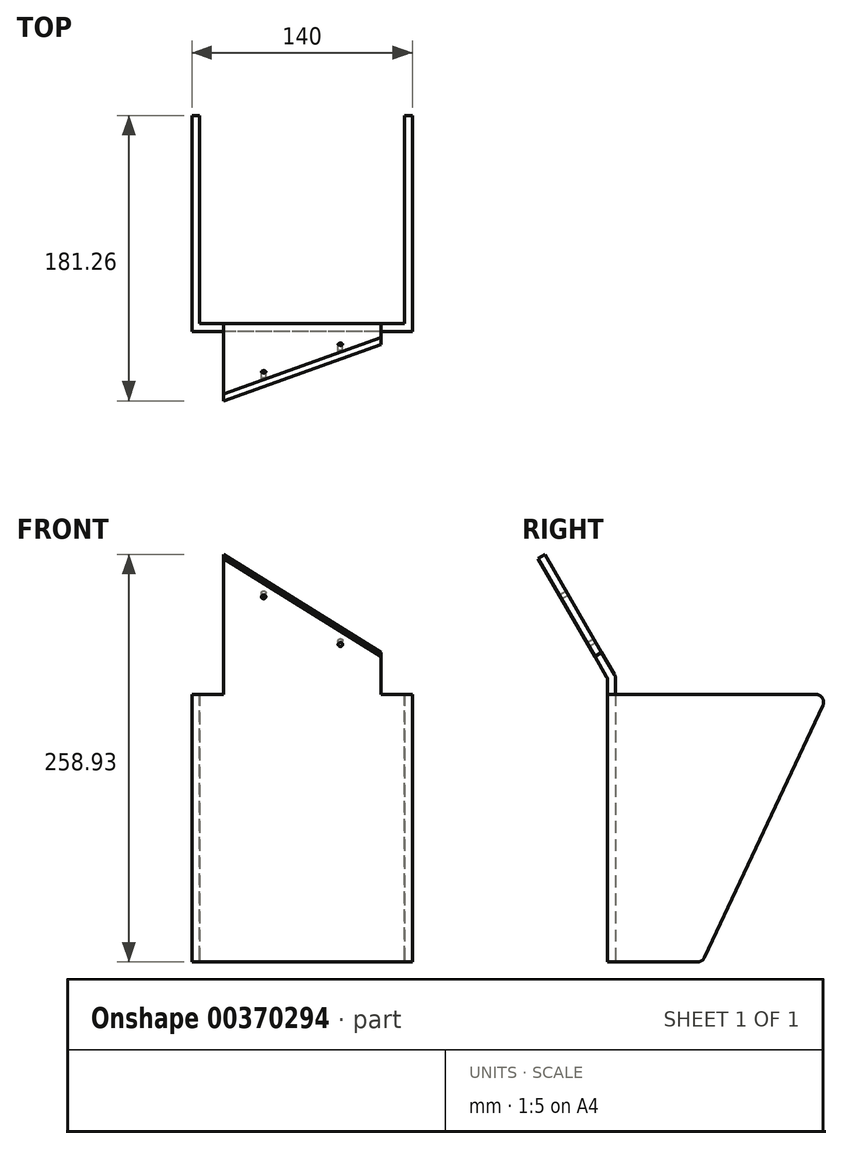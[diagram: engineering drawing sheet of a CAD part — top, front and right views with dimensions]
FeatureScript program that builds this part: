
annotation { "Feature Type Name" : "Feature", "Feature Type Description" : "" }
export const myFeature = defineFeature(function(context is Context, id is Id, definition is map)
    precondition{}
    {
        {
            var Q0;
            Q0=qCreatedBy(makeId("Top.planeOp"),FACE);
            var sketch = newSketch(context, id + "F0", { "sketchPlane" : qUnion([Q0])});
            skLineSegment(sketch, "E0.bottom", {"start": v(70, 0) * mm, "end": v(-70, 0) * mm});
            skLineSegment(sketch, "E0.top", {"start": v(70, 140) * mm, "end": v(65, 140) * mm});
            skLineSegment(sketch, "E0.left", {"start": v(70, 0) * mm, "end": v(70, 140) * mm});
            skLineSegment(sketch, "E0.right", {"start": v(-70, 0) * mm, "end": v(-70, 140) * mm});
            skLineSegment(sketch, "E1", {"start": v(-65, 140) * mm, "end": v(-65, 5) * mm});
            skLineSegment(sketch, "E2", {"start": v(65, 140) * mm, "end": v(65, 5) * mm});
            skLineSegment(sketch, "E3", {"start": v(-65, 5) * mm, "end": v(65, 5) * mm});
            skLineSegment(sketch, "E4.trimOffspring", {"start": v(-65, 140) * mm, "end": v(-70, 140) * mm});
            skPoint(sketch, "E5.orphan", {"position": v(-65, 0) * mm});
            skPoint(sketch, "E6.orphan", {"position": v(65, 0) * mm});
            skSolve(sketch);
        }
        {
            var Q0;
            Q0 = qSketchRegion(id + "F0", true);
            extrude(context, id + "F1", {"entities" : qUnion([Q0]), "depth" : 270 * mm});
        }
        {
            var Q0;
            Q0=qCreatedBy(makeId("Right.planeOp"),FACE);
            var sketch = newSketch(context, id + "F2", { "sketchPlane" : qUnion([Q0])});
            skLineSegment(sketch, "E7", {"start": v(140, 170) * mm, "end": v(140, 0) * mm});
            skLineSegment(sketch, "E8", {"start": v(140, 0) * mm, "end": v(60.1, 0) * mm});
            skLineSegment(sketch, "E9", {"start": v(61.45, 2.87) * mm, "end": v(136.65, 162.87) * mm});
            skPoint(sketch, "E10.visualSharp", {"position": v(140, 170) * mm});
            skArc(sketch, "E10.filletArc", {"start": v(136.65, 162.87) * mm, "mid": v(136.35, 167.68) * mm, "end": v(132.13, 170) * mm});
            skLineSegment(sketch, "E11", {"start": v(132.13, 170) * mm, "end": v(140, 170) * mm});
            skPoint(sketch, "E12.visualSharp", {"position": v(60.1, 0) * mm});
            skArc(sketch, "E12.filletArc", {"start": v(56.92, 0) * mm, "mid": v(59.6, 0.78) * mm, "end": v(61.45, 2.87) * mm});
            skLineSegment(sketch, "E13", {"start": v(56.92, 0) * mm, "end": v(60.1, 0) * mm});
            skLineSegment(sketch, "E14.bottom", {"start": v(140, 170) * mm, "end": v(0, 170) * mm});
            skLineSegment(sketch, "E14.top", {"start": v(140, 280.33) * mm, "end": v(0, 280.33) * mm});
            skLineSegment(sketch, "E14.left", {"start": v(140, 170) * mm, "end": v(140, 280.33) * mm});
            skLineSegment(sketch, "E14.right", {"start": v(0, 170) * mm, "end": v(0, 280.33) * mm});
            skSolve(sketch);
        }
        {
            var Q0;
            Q0 = qSketchRegion(id + "F2", true);
            extrude(context, id + "F3", {"entities" : qUnion([Q0]), "operationType" : NewBodyOperationType.REMOVE, "endBound" : BoundingType.SYMMETRIC, "oppositeDirection" : true, "depth" : 500 * mm});
        }
        {
            var Q0;
            Q0=qCreatedBy(makeId("Right.planeOp"),FACE);
            var sketch = newSketch(context, id + "F4", { "sketchPlane" : qUnion([Q0])});
            skLineSegment(sketch, "E15.bottom", {"start": v(0, 170) * mm, "end": v(5, 170) * mm});
            skLineSegment(sketch, "E15.left", {"start": v(0, 170) * mm, "end": v(0, 178.66) * mm});
            skLineSegment(sketch, "E15.right", {"start": v(5, 170) * mm, "end": v(5, 180) * mm});
            skLineSegment(sketch, "E16", {"start": v(-0.67, 181.16) * mm, "end": v(-53, 271.8) * mm});
            skLineSegment(sketch, "E17", {"start": v(-53, 271.8) * mm, "end": v(-48.68, 274.3) * mm});
            skLineSegment(sketch, "E18", {"start": v(-48.68, 274.3) * mm, "end": v(4.33, 182.5) * mm});
            skPoint(sketch, "E19.visualSharp", {"position": v(0, 180) * mm});
            skArc(sketch, "E19.filletArc", {"start": v(0, 178.66) * mm, "mid": v(-0.17, 179.95) * mm, "end": v(-0.67, 181.16) * mm});
            skPoint(sketch, "E20.visualSharp", {"position": v(5, 181.34) * mm});
            skArc(sketch, "E20.filletArc", {"start": v(5, 180) * mm, "mid": v(4.83, 181.3) * mm, "end": v(4.33, 182.5) * mm});
            skSolve(sketch);
        }
        {
            var Q0;
            Q0 = qSketchRegion(id + "F4", true);
            extrude(context, id + "F5", {"entities" : qUnion([Q0]), "operationType" : NewBodyOperationType.ADD, "endBound" : BoundingType.SYMMETRIC, "depth" : 100 * mm});
        }
        {
            var Q0;
            Q0=makeQuery(id+"F5.opExtrude","SWEPT_FACE",FACE,{"disambiguationData":[OSD([sQuery(id+"F4.wireOp",EDGE,"E18")])]});
            var sketch = newSketch(context, id + "F6", { "sketchPlane" : qUnion([Q0])});
            skCircle(sketch, "E21", {"center": v(-24.37, 180.88) * mm, "radius": 1.4 * mm});
            skCircle(sketch, "E22", {"center": v(24.37, 215.88) * mm, "radius": 1.4 * mm});
            skLineSegment(sketch, "E23", {"start": v(-50, 172.32) * mm, "end": v(50, 244.14) * mm});
            skLineSegment(sketch, "E24", {"start": v(50, 244.14) * mm, "end": v(50, 285.77) * mm});
            skLineSegment(sketch, "E25", {"start": v(50, 285.77) * mm, "end": v(-50, 285.77) * mm});
            skLineSegment(sketch, "E26", {"start": v(-50, 285.77) * mm, "end": v(-50, 172.32) * mm});
            skLineSegment(sketch, "E27", {"start": v(-24.37, 180.88) * mm, "end": v(24.37, 215.88) * mm});
            skPoint(sketch, "E28", {"position": v(0, 198.38) * mm});
            skPoint(sketch, "E29", {"position": v(0, 261.9) * mm});
            skSolve(sketch);
        }
        {
            var Q0;
            Q0 = qSketchRegion(id + "F6", true);
            extrude(context, id + "F7", {"entities" : qUnion([Q0]), "operationType" : NewBodyOperationType.REMOVE, "oppositeDirection" : true, "depth" : 25 * mm});
        }
    });
